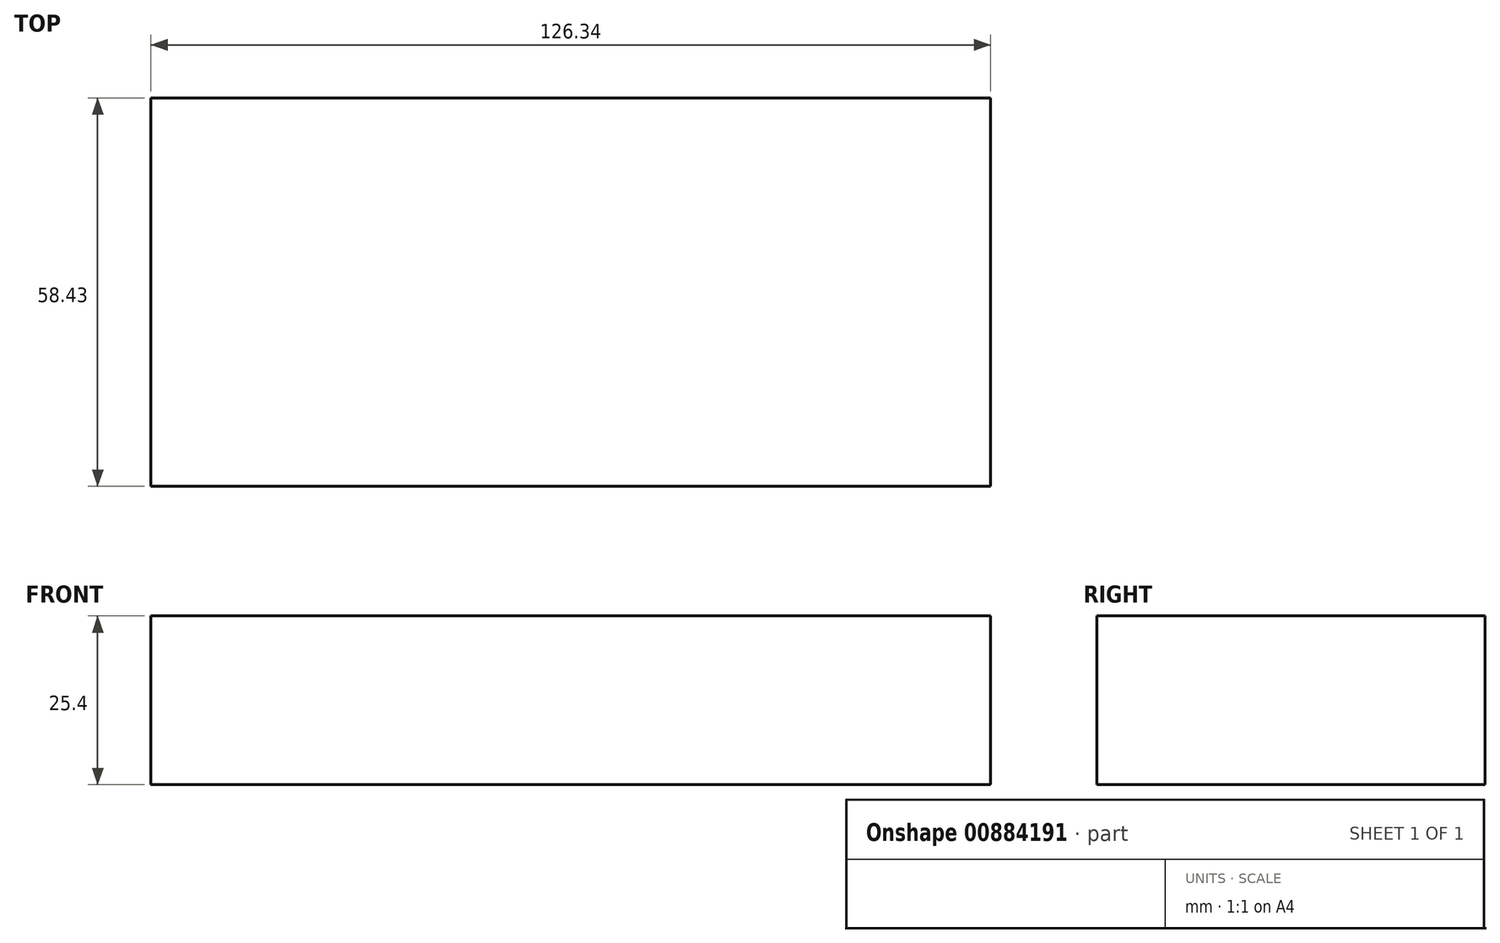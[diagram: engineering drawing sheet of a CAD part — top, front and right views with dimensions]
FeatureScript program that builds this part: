
annotation { "Feature Type Name" : "Feature", "Feature Type Description" : "" }
export const myFeature = defineFeature(function(context is Context, id is Id, definition is map)
    precondition{}
    {
        {
            var Q0;
            Q0=qCreatedBy(makeId("Top.planeOp"),FACE);
            var sketch = newSketch(context, id + "F0", { "sketchPlane" : qUnion([Q0])});
            skLineSegment(sketch, "E0.bottom", {"start": v(0, 0) * mm, "end": v(126.34, 0) * mm});
            skLineSegment(sketch, "E0.top", {"start": v(0, -58.43) * mm, "end": v(126.34, -58.43) * mm});
            skLineSegment(sketch, "E0.left", {"start": v(0, 0) * mm, "end": v(0, -58.43) * mm});
            skLineSegment(sketch, "E0.right", {"start": v(126.34, 0) * mm, "end": v(126.34, -58.43) * mm});
            skSolve(sketch);
        }
        {
            var Q0;
            Q0 = qSketchRegion(id + "F0", true);
            extrude(context, id + "F1", {"entities" : qUnion([Q0]), "depth" : 25.4 * mm, "offsetDistance" : 25.4 * mm});
        }
    });
